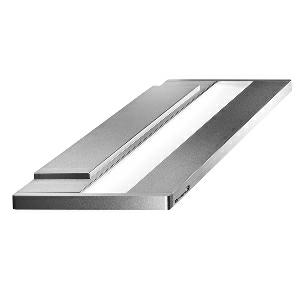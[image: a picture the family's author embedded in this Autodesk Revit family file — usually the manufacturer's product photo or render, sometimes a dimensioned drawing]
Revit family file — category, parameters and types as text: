
# Revit family: zera_bed_-_zew_9000_830_-_ul_li_nl_00812993_9c04
name_source: partatom
category: Lighting Fixtures
units: mm (PartAtom-declared; Revit-internal decimal feet)

## family parameters
Cut with Voids When Loaded = No
Host = Face
Light Source = No
Part Type = Normal
Room Calculation Point = No
Round Connector Dimension = Use Diameter
Shared = No

## types (1)
- AL+UL (1 x LED, 7600 lm, 4000K/3000K)
    Apparent Load = 76 VA
    Approval mark = CE
    CIE Flux Codes = 45 81 99 31 100
    Color Rendering = 90/80
    Color Temperature = 4000K/3000K
    Default Elevation = 2000 mm  [stored 6.56168 ft]
    Description = ZEW 9000/830|Wall-mounted luminaire|light source:   Warm white   |work equipment: Power supply unit|luminous flux: 8960 lm|light distribution: Direct/indirect|class of protection: I|technology: Switchable|mains lead: Connector 5 pin|glare control: Diffusor|special features: General light, indirect, 3000K, Ra80, DIN EN 60598-2-25, Reading light, direct, 2700K, Ra90, indir, Switch left, dir 4K 36W Ra95|
    Frequency = 50 Hz, 60 Hz
    Height = 20 mm  [stored 0.0656168 ft]
    Lamp = 1 x LED
    Lamp Light Flux = 7600 lm
    Lamp count = 1
    Length = 1050 mm
    Luminous efficacy = 100 lm/W
    Manufacturer = Waldmann
    ModVariant = No
    Model = 00812993
    Mounting Place = Wall
    Mounting Type = Surface mounted
    Number of Poles = 1
    OnlyDefault = Yes
    Power Factor = 1
    Product Name = ZERA.bed - ZEW 9000/830 - UL LI/NL
    Product group = Wall mounted Luminaire
    ProductGroupID = 20
    Protection Class = Protection class I
    Protection Degree = IP 20
    RLX_Detail_Level = 1
    RLX_Emergency_Light_Flux = 0 lm
    RLX_Emergency_Type = 0
    RLX_Emergency_Type_DB = No
    RlxData = <blob elided: 62733 chars, md5=d6b0b1fa>
    Socket = socket
    Standby Power = 0 W
    System Light Flux = 7600 lm
    System Power = 76 W
    Type Comments = General and Examation Light
    Type Image = zera_bed.jpg
    URL = http://relux.com
    VarID = al_ul_37f9
    Voltage = 230 V
    Voltage Range = 220-240 V
    Weight = 0.00 kg
    Width = 230 mm

note: [stored X ft] marks values corroborated as IEEE doubles in the binary element streams (Revit-internal decimal feet)

## geometry (parser evidence)
native form markers: Blend x4, Sweep x11
no freeform markers — native parametric forms only
